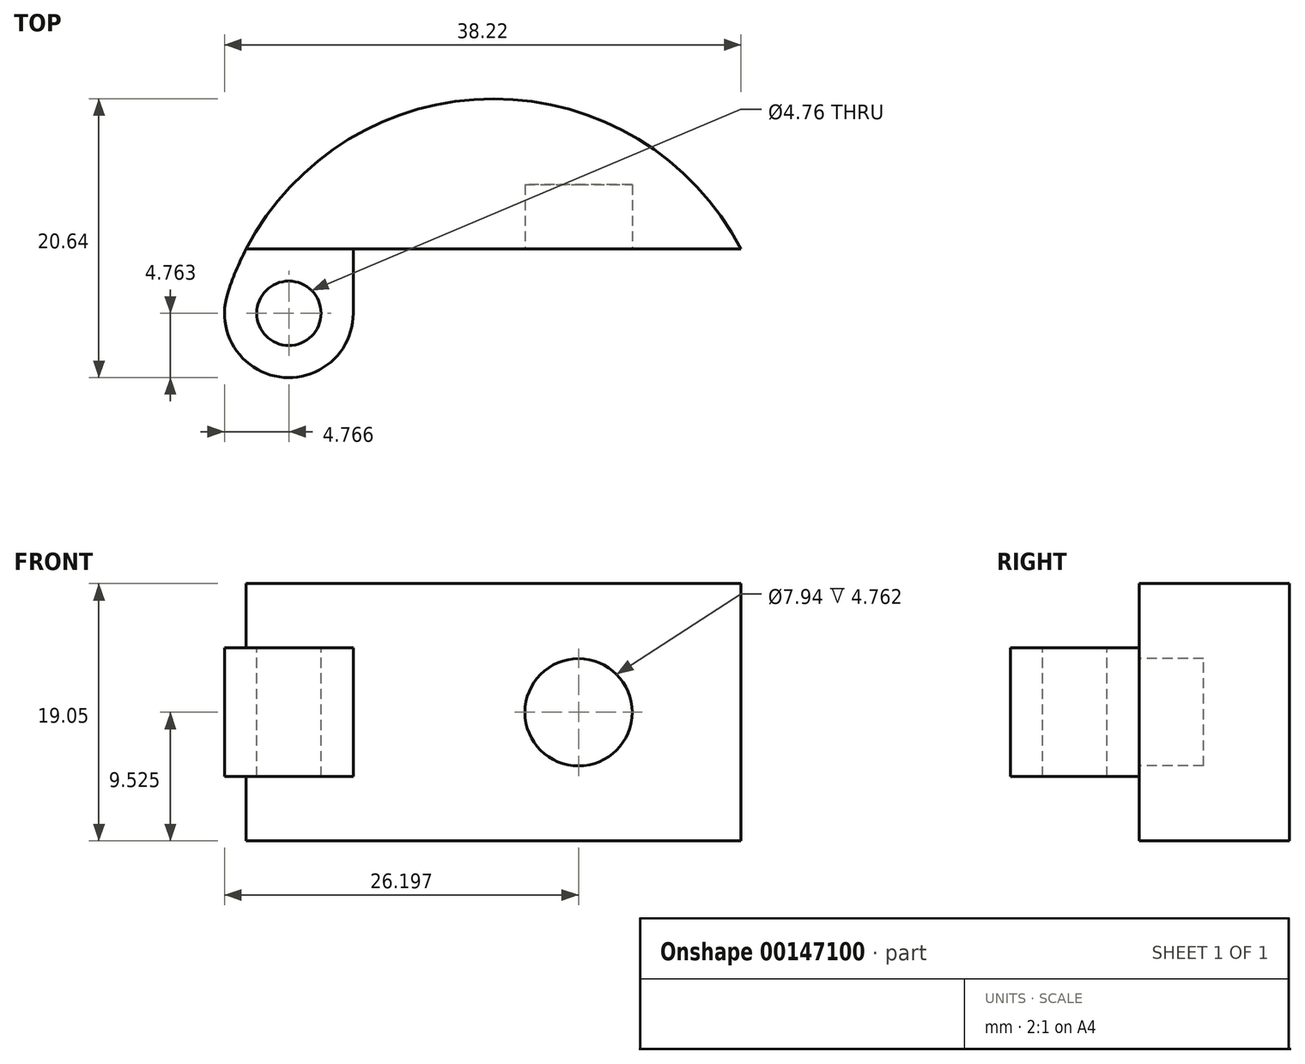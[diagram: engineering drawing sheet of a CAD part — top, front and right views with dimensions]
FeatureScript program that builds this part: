
annotation { "Feature Type Name" : "Feature", "Feature Type Description" : "" }
export const myFeature = defineFeature(function(context is Context, id is Id, definition is map)
    precondition{}
    {
        {
            var Q0;
            Q0=qCreatedBy(makeId("Top.planeOp"),FACE);
            var sketch = newSketch(context, id + "F0", { "sketchPlane" : qUnion([Q0])});
            skLineSegment(sketch, "E0", {"start": v(35.12, 12.42) * mm, "end": v(35.12, 12.42) * mm});
            skArc(sketch, "E1", {"start": v(18.3, 9.53) * mm, "mid": v(-1.8, 20.56) * mm, "end": v(-19.69, 6.2) * mm});
            skLineSegment(sketch, "E2", {"start": v(-10.38, 9.53) * mm, "end": v(18.3, 9.53) * mm});
            skArc(sketch, "E3", {"start": v(-19.69, 6.2) * mm, "mid": v(-15.87, 0.06) * mm, "end": v(-10.38, 4.76) * mm});
            skLineSegment(sketch, "E4", {"start": v(-10.38, 4.76) * mm, "end": v(-10.38, 9.53) * mm});
            skPoint(sketch, "E5.orphan", {"position": v(-20.59, -1.41) * mm});
            skSolve(sketch);
        }
        {
            var Q0;
            Q0=makeQuery(id+"F0.imprint","IMPRINT",FACE,{"disambiguationData":[TD([[makeQuery(id+"F0.imprint","IMPRINT",EDGE,{"derivedFrom":sQuery(id+"F0.wireOp",EDGE,"E1")}),1.0]])]});
            extrude(context, id + "F1", {"entities" : qUnion([Q0]), "depth" : 19.05 * mm});
        }
        {
            var Q0;
            Q0=makeQuery(id+"F1.opExtrude","SWEPT_FACE",FACE,{"disambiguationData":[OSD([sQuery(id+"F0.wireOp",EDGE,"E4")])]});
            var sketch = newSketch(context, id + "F2", { "sketchPlane" : qUnion([Q0])});
            skLineSegment(sketch, "E6.bottom", {"start": v(9.53, 19.05) * mm, "end": v(0, 19.05) * mm});
            skLineSegment(sketch, "E6.top", {"start": v(9.53, 14.29) * mm, "end": v(0, 14.29) * mm});
            skLineSegment(sketch, "E6.left", {"start": v(9.53, 19.05) * mm, "end": v(9.53, 14.29) * mm});
            skLineSegment(sketch, "E6.right", {"start": v(0, 19.05) * mm, "end": v(0, 14.29) * mm});
            skLineSegment(sketch, "E7.bottom", {"start": v(9.53, 0) * mm, "end": v(0, 0) * mm});
            skLineSegment(sketch, "E7.top", {"start": v(9.53, 4.76) * mm, "end": v(0, 4.76) * mm});
            skLineSegment(sketch, "E7.left", {"start": v(9.53, 0) * mm, "end": v(9.53, 4.76) * mm});
            skLineSegment(sketch, "E7.right", {"start": v(0, 0) * mm, "end": v(0, 4.76) * mm});
            skSolve(sketch);
        }
        {
            var Q0;
            {var subQ0=sQuery(id+"F2.wireOp",EDGE,"E6.left");Q0=makeQuery(id+"F2.imprint","IMPRINT",FACE,{"disambiguationData":[TD([[makeQuery(id+"F2.imprint","IMPRINT",EDGE,{"derivedFrom":subQ0}),-1.0]])]});}
            var Q1;
            {var subQ3=sQuery(id+"F2.wireOp",EDGE,"E6.right");Q1=makeQuery(id+"F2.imprint","IMPRINT",FACE,{"disambiguationData":[TD([[makeQuery(id+"F2.imprint","IMPRINT",EDGE,{"derivedFrom":subQ3}),1.0]])]});}
            var Q2;
            {var subQ0=sQuery(id+"F2.wireOp",EDGE,"E7.left");Q2=makeQuery(id+"F2.imprint","IMPRINT",FACE,{"disambiguationData":[TD([[makeQuery(id+"F2.imprint","IMPRINT",EDGE,{"derivedFrom":subQ0}),-1.0]])]});}
            var Q3;
            {var subQ3=sQuery(id+"F2.wireOp",EDGE,"E7.right");Q3=makeQuery(id+"F2.imprint","IMPRINT",FACE,{"disambiguationData":[TD([[makeQuery(id+"F2.imprint","IMPRINT",EDGE,{"derivedFrom":subQ3}),-1.0]])]});}
            extrude(context, id + "F3", {"entities" : qUnion([Q0, Q1, Q2, Q3]), "operationType" : NewBodyOperationType.REMOVE, "oppositeDirection" : true, "depth" : 25.4 * mm});
        }
        {
            var Q0;
            Q0=makeQuery(id+"F3.boolean.opBoolean","COPY",FACE,{"derivedFrom":makeQuery(id+"F3.opExtrude","SWEPT_FACE",FACE,{"disambiguationData":[OSD([sQuery(id+"F2.wireOp",EDGE,"E6.top")])]})});
            var sketch = newSketch(context, id + "F4", { "sketchPlane" : qUnion([Q0])});
            skCircle(sketch, "E8", {"center": v(-15.14, 4.76) * mm, "radius": 2.38 * mm});
            skSolve(sketch);
        }
        {
            var Q0;
            Q0 = qSketchRegion(id + "F4", true);
            extrude(context, id + "F5", {"entities" : qUnion([Q0]), "operationType" : NewBodyOperationType.REMOVE, "endBound" : BoundingType.THROUGH_ALL, "oppositeDirection" : true, "depth" : 25.4 * mm});
        }
        {
            var Q0;
            Q0=makeQuery(id+"F3.boolean.opBoolean","MERGE",FACE,{"derivedFrom":[makeQuery(id+"F1.opExtrude","SWEPT_FACE",FACE,{"disambiguationData":[OSD([sQuery(id+"F0.wireOp",EDGE,"E2")])]}),makeQuery(id+"F3.opExtrude","SWEPT_FACE",FACE,{"disambiguationData":[OSD([sQuery(id+"F2.wireOp",EDGE,"E6.left")])]}),makeQuery(id+"F3.opExtrude","SWEPT_FACE",FACE,{"disambiguationData":[OSD([sQuery(id+"F2.wireOp",EDGE,"E7.left")])]})]});
            var sketch = newSketch(context, id + "F6", { "sketchPlane" : qUnion([Q0])});
            skCircle(sketch, "E9", {"center": v(6.29, 9.53) * mm, "radius": 3.97 * mm});
            skSolve(sketch);
        }
        {
            var Q0;
            Q0=makeQuery(id+"F6.imprint","IMPRINT",FACE,{"disambiguationData":[TD([[makeQuery(id+"F6.imprint","IMPRINT",EDGE,{"derivedFrom":sQuery(id+"F6.wireOp",EDGE,"E9")}),1.0]])]});
            extrude(context, id + "F7", {"entities" : qUnion([Q0]), "operationType" : NewBodyOperationType.REMOVE, "oppositeDirection" : true, "depth" : 4.76 * mm});
        }
    });
